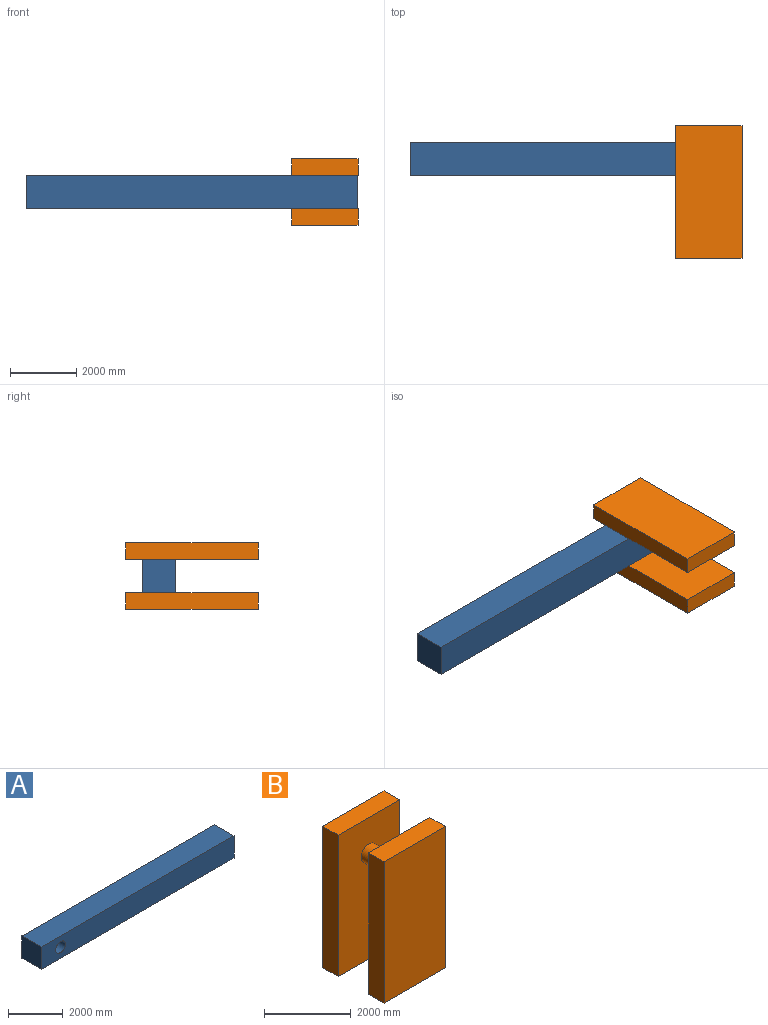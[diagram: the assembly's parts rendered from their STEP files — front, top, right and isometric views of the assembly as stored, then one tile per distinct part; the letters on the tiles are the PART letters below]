
ASSEMBLY  parts=2 mates=1
PART A: 7 faces, bbox 10000x1000x1000 mm
  f0: plane 10000x1000mm, normal (0,0,1), area 10000000mm2, adj f1,f3,f4,f5
  f1: plane 1000x1000mm, normal (-1,0,0), area 1000000mm2, adj f0,f2,f4,f5
  f2: plane 10000x1000mm, normal (0,0,-1), area 10000000mm2, adj f1,f3,f4,f5
  f3: plane 1000x1000mm, normal (1,0,0), area 1000000mm2, adj f0,f2,f4,f5
  f4: plane 10000x1000mm, normal (0,-1,0), area 9803650.5mm2, adj f0,f1,f2,f3,f6
  f5: plane 10000x1000mm, normal (0,1,0), area 9803650.5mm2, adj f0,f1,f2,f3,f6
  f6: cylinder r=250mm len=1000mm, axis (0,-1,0), area 1570796.3mm2, adj f4,f5
PART B: 13 faces, bbox 2000x2000x4000 mm
  f0: plane 2000x500mm, normal (0,0,1), area 1000000mm2, adj f1,f3,f4,f5
  f1: plane 4000x500mm, normal (-1,0,0), area 2000000mm2, adj f0,f2,f4,f5
  f2: plane 2000x500mm, normal (0,0,-1), area 1000000mm2, adj f1,f3,f4,f5
  f3: plane 4000x500mm, normal (1,0,0), area 2000000mm2, adj f0,f2,f4,f5
  f4: plane 4000x2000mm, normal (0,-1,0), area 7803650.5mm2, adj f0,f1,f2,f3,f6
  f5: plane 4000x2000mm, normal (0,1,0), area 8000000mm2, adj f0,f1,f2,f3
  f6: cylinder r=250mm len=1000mm, axis (0,1,0), area 1570796.3mm2, adj f4,f12
  f7: plane 2000x500mm, normal (0,0,1), area 1000000mm2, adj f8,f10,f11,f12
  f8: plane 4000x500mm, normal (-1,0,0), area 2000000mm2, adj f7,f9,f11,f12
  f9: plane 2000x500mm, normal (0,0,-1), area 1000000mm2, adj f8,f10,f11,f12
  f10: plane 4000x500mm, normal (1,0,0), area 2000000mm2, adj f7,f9,f11,f12
  f11: plane 4000x2000mm, normal (0,-1,0), area 8000000mm2, adj f7,f8,f9,f10
  f12: plane 4000x2000mm, normal (0,1,0), area 7803650.5mm2, adj f6,f7,f8,f9,f10
PLACE A rot(axis=(0,0.71,-0.71),180deg) t=(175.94,3352.58,-3210.6)mm
PLACE B rot(axis=(-1,0,0),90deg) t=(-1824.06,-147.42,-3710.6)mm fixed
MATE revolute B.f6 <-> A.f6  axis (0,0,1) through (-824.06,2852.58,-3210.6)mm
